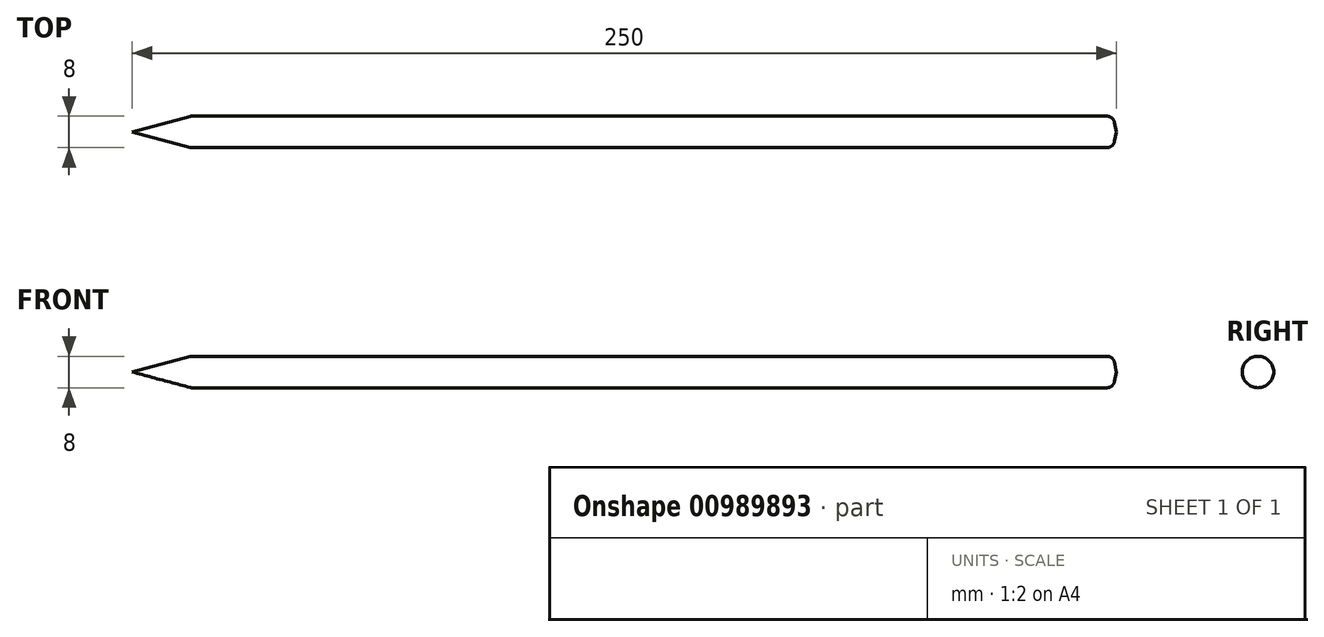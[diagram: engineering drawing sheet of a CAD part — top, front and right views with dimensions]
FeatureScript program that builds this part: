
annotation { "Feature Type Name" : "Feature", "Feature Type Description" : "" }
export const myFeature = defineFeature(function(context is Context, id is Id, definition is map)
    precondition{}
    {
        {
            var Q0;
            Q0=qCreatedBy(makeId("Top.planeOp"),FACE);
            var sketch = newSketch(context, id + "F0", { "sketchPlane" : qUnion([Q0])});
            skLineSegment(sketch, "E0", {"start": v(0, 0) * mm, "end": v(250, 0) * mm});
            skLineSegment(sketch, "E1", {"start": v(0, 0) * mm, "end": v(14.93, 4) * mm});
            skLineSegment(sketch, "E2", {"start": v(14.93, 4) * mm, "end": v(249.3, 4) * mm});
            skLineSegment(sketch, "E3", {"start": v(249.3, 4) * mm, "end": v(250, 0) * mm});
            skSolve(sketch);
        }
        {
            var Q0;
            Q0=makeQuery(id+"F0.imprint","IMPRINT",FACE,{"disambiguationData":[TD([[makeQuery(id+"F0.imprint","IMPRINT",EDGE,{"derivedFrom":sQuery(id+"F0.wireOp",EDGE,"E0")}),1.0]])]});
            var Q1;
            Q1=sQuery(id+"F0.wireOp",EDGE,"E0");
            revolve(context, id + "F1", {"surfaceOperationType" : NewSurfaceOperationType.NEW, "entities" : qUnion([Q0]), "axis" : qUnion([Q1]), "revolveType" : RevolveType.FULL});
        }
        {
            var Q0;
            Q0=makeQuery(id+"F1.opRevolve","SWEPT_EDGE",EDGE,{"disambiguationData":[OSD([sQuery(id+"F0.wireOp",EDGE,"E1"),sQuery(id+"F0.wireOp",EDGE,"E2")])]});
            var Q1;
            Q1=makeQuery(id+"F1.opRevolve","SWEPT_EDGE",EDGE,{"disambiguationData":[OSD([sQuery(id+"F0.wireOp",EDGE,"E2"),sQuery(id+"F0.wireOp",EDGE,"E3")])]});
            fillet(context, id + "F2", {"entities" : qUnion([Q0, Q1]), "radius" : 2 * mm, "tangentPropagation" : true, "allowEdgeOverflow" : false});
        }
    });
